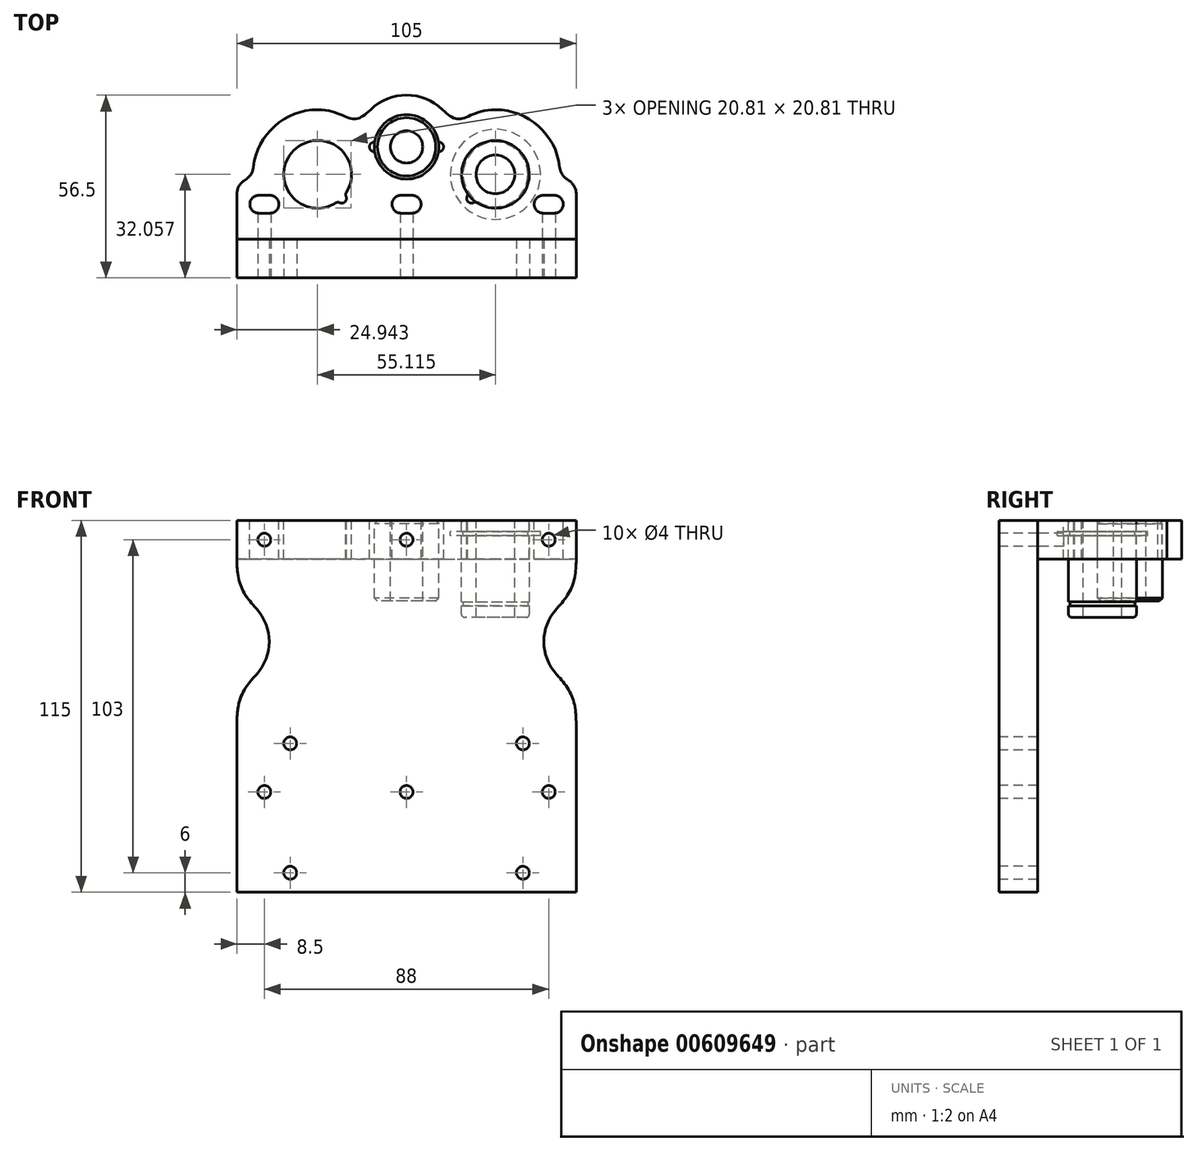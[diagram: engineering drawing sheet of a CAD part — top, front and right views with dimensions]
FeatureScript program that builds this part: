
annotation { "Feature Type Name" : "Feature", "Feature Type Description" : "" }
export const myFeature = defineFeature(function(context is Context, id is Id, definition is map)
    precondition{}
    {
        {
            var Q0;
            Q0=qCreatedBy(makeId("Front.planeOp"),FACE);
            var sketch = newSketch(context, id + "F0", { "sketchPlane" : qUnion([Q0])});
            skLineSegment(sketch, "E0.bottom", {"start": v(-52.5, 0) * mm, "end": v(52.5, 0) * mm});
            skLineSegment(sketch, "E0.top", {"start": v(-52.5, 90) * mm, "end": v(52.5, 90) * mm});
            skLineSegment(sketch, "E0.left", {"start": v(-52.5, 0) * mm, "end": v(-52.5, 90) * mm});
            skLineSegment(sketch, "E0.right", {"start": v(52.5, 0) * mm, "end": v(52.5, 90) * mm});
            skSolve(sketch);
        }
        {
            var Q0;
            Q0=qSketchRegion(id+"F0",true);
            extrude(context, id + "F1", {"entities" : qUnion([Q0]), "oppositeDirection" : true, "depth" : 12 * mm, "offsetDistance" : 25 * mm});
        }
        {
            var Q0;
            Q0=makeQuery(id+"F1.opExtrude","SWEPT_FACE",FACE,{"disambiguationData":[OSD([sQuery(id+"F0.wireOp",EDGE,"E0.top")])]});
            var sketch = newSketch(context, id + "F2", { "sketchPlane" : qUnion([Q0])});
            skLineSegment(sketch, "E1.top", {"start": v(27.5, 52) * mm, "end": v(11.12, 52) * mm, "construction": true});
            skLineSegment(sketch, "E2", {"start": v(0, 12) * mm, "end": v(0, 52) * mm, "construction": true});
            skPoint(sketch, "E3.centerSnap0", {"position": v(0, 32) * mm});
            skArc(sketch, "E4.filletArc", {"start": v(47.5, 32) * mm, "mid": v(41.64, 46.14) * mm, "end": v(27.5, 52) * mm});
            skArc(sketch, "E5.filletArc", {"start": v(-27.5, 52) * mm, "mid": v(-41.64, 46.14) * mm, "end": v(-47.5, 32) * mm});
            skArc(sketch, "E6", {"start": v(21.8, 23.22) * mm, "mid": v(34.9, 39.4) * mm, "end": v(18.72, 26.3) * mm});
            skArc(sketch, "E7.MirrorC", {"start": v(-21.8, 23.22) * mm, "mid": v(-34.9, 39.4) * mm, "end": v(-18.72, 26.3) * mm});
            skArc(sketch, "E8", {"start": v(11.12, 52) * mm, "mid": v(0, 56.5) * mm, "end": v(-11.12, 52) * mm});
            skArc(sketch, "E9", {"start": v(-9.74, 38.33) * mm, "mid": v(0, 30.53) * mm, "end": v(9.74, 38.33) * mm});
            skLineSegment(sketch, "E10", {"start": v(47.5, 12) * mm, "end": v(-47.5, 12) * mm});
            skLineSegment(sketch, "E11.bottom", {"start": v(47.5, 32) * mm, "end": v(52.5, 28.5) * mm});
            skLineSegment(sketch, "E11.top", {"start": v(47.5, 12) * mm, "end": v(52.5, 12) * mm});
            skLineSegment(sketch, "E11.right", {"start": v(52.5, 28.5) * mm, "end": v(52.5, 12) * mm});
            skLineSegment(sketch, "E12.bottom", {"start": v(42.25, 25.5) * mm, "end": v(45.75, 25.5) * mm});
            skLineSegment(sketch, "E12.top", {"start": v(42.25, 20) * mm, "end": v(45.75, 20) * mm});
            skArc(sketch, "E13", {"start": v(42.25, 25.5) * mm, "mid": v(39.5, 22.75) * mm, "end": v(42.25, 20) * mm});
            skArc(sketch, "E14", {"start": v(45.75, 20) * mm, "mid": v(48.5, 22.75) * mm, "end": v(45.75, 25.5) * mm});
            skArc(sketch, "E15.MirrorCS", {"start": v(-42.25, 25.5) * mm, "mid": v(-39.5, 22.75) * mm, "end": v(-42.25, 20) * mm});
            skLineSegment(sketch, "E16.MirrorCS", {"start": v(-42.25, 25.5) * mm, "end": v(-45.75, 25.5) * mm});
            skLineSegment(sketch, "E17.MirrorCS", {"start": v(-42.25, 20) * mm, "end": v(-45.75, 20) * mm});
            skArc(sketch, "E18.MirrorCS", {"start": v(-45.75, 20) * mm, "mid": v(-48.5, 22.75) * mm, "end": v(-45.75, 25.5) * mm});
            skLineSegment(sketch, "E19.MirrorCS", {"start": v(-47.5, 32) * mm, "end": v(-52.5, 28.5) * mm});
            skLineSegment(sketch, "E20.MirrorCS", {"start": v(-52.5, 28.5) * mm, "end": v(-52.5, 12) * mm});
            skLineSegment(sketch, "E21.MirrorCS", {"start": v(-47.5, 12) * mm, "end": v(-52.5, 12) * mm});
            skLineSegment(sketch, "E22.bottom", {"start": v(-1.75, 25.5) * mm, "end": v(1.75, 25.5) * mm});
            skLineSegment(sketch, "E22.top", {"start": v(-1.75, 20) * mm, "end": v(1.75, 20) * mm});
            skArc(sketch, "E23", {"start": v(-1.75, 25.5) * mm, "mid": v(-4.5, 22.75) * mm, "end": v(-1.75, 20) * mm});
            skArc(sketch, "E24", {"start": v(1.75, 20) * mm, "mid": v(4.5, 22.75) * mm, "end": v(1.75, 25.5) * mm});
            skLineSegment(sketch, "E25", {"start": v(-1.75, 22.75) * mm, "end": v(1.75, 22.75) * mm, "construction": true});
            skPoint(sketch, "E26", {"position": v(0, 22.75) * mm});
            skLineSegment(sketch, "E27", {"start": v(-44, 25.5) * mm, "end": v(-44, 20) * mm, "construction": true});
            skLineSegment(sketch, "E28", {"start": v(44, 20) * mm, "end": v(44, 25.5) * mm, "construction": true});
            skLineSegment(sketch, "E29.trimOffspring", {"start": v(-11.12, 52) * mm, "end": v(-27.5, 52) * mm, "construction": true});
            skFitSpline(sketch, "E30", {"points": [v(11.12, 52) * mm, v(16.56, 49.16) * mm, v(27.5, 52) * mm], "startDerivative": vector(14.38, -13.9) * mm, "endDerivative": vector(29.13, 0) * mm});
            skFitSpline(sketch, "E31.MirrorCS", {"points": [v(-11.12, 52) * mm, v(-16.56, 49.16) * mm, v(-27.5, 52) * mm], "startDerivative": vector(-14.38, -13.9) * mm, "endDerivative": vector(-29.13, 0) * mm});
            skLineSegment(sketch, "E32", {"start": v(-11.12, 52) * mm, "end": v(11.12, 52) * mm, "construction": true});
            skArc(sketch, "E33", {"start": v(-10.42, 41.93) * mm, "mid": v(-11.47, 40.5) * mm, "end": v(-10.42, 39.07) * mm});
            skArc(sketch, "E34.MirrorC", {"start": v(10.42, 41.93) * mm, "mid": v(11.47, 40.5) * mm, "end": v(10.42, 39.07) * mm});
            skArc(sketch, "E35.trimOffspring", {"start": v(9.74, 42.67) * mm, "mid": v(0, 50.48) * mm, "end": v(-9.74, 42.67) * mm});
            skPoint(sketch, "E36.visualSharp", {"position": v(-9.86, 42) * mm});
            skArc(sketch, "E36.filletArc", {"start": v(-10.42, 41.93) * mm, "mid": v(-9.98, 42.21) * mm, "end": v(-9.74, 42.67) * mm});
            skPoint(sketch, "E37.visualSharp", {"position": v(-9.86, 39) * mm});
            skArc(sketch, "E37.filletArc", {"start": v(-9.74, 38.33) * mm, "mid": v(-9.98, 38.79) * mm, "end": v(-10.42, 39.07) * mm});
            skPoint(sketch, "E38.visualSharp", {"position": v(9.86, 39) * mm});
            skArc(sketch, "E38.filletArc", {"start": v(10.42, 39.07) * mm, "mid": v(9.98, 38.79) * mm, "end": v(9.74, 38.33) * mm});
            skPoint(sketch, "E39.visualSharp", {"position": v(9.86, 42) * mm});
            skArc(sketch, "E39.filletArc", {"start": v(9.74, 42.67) * mm, "mid": v(9.98, 42.21) * mm, "end": v(10.42, 41.93) * mm});
            skArc(sketch, "E40", {"start": v(-20.79, 23.26) * mm, "mid": v(-19.03, 23.53) * mm, "end": v(-18.76, 25.29) * mm});
            skLineSegment(sketch, "E41", {"start": v(-27.5, 32) * mm, "end": v(-20.1, 24.6) * mm, "construction": true});
            skArc(sketch, "E42.MirrorCS", {"start": v(20.79, 23.26) * mm, "mid": v(19.03, 23.53) * mm, "end": v(18.76, 25.29) * mm});
            skPoint(sketch, "E43.visualSharp", {"position": v(-21.23, 23.61) * mm});
            skArc(sketch, "E43.filletArc", {"start": v(-20.79, 23.26) * mm, "mid": v(-21.3, 23.38) * mm, "end": v(-21.8, 23.22) * mm});
            skPoint(sketch, "E44.visualSharp", {"position": v(-19.11, 25.73) * mm});
            skArc(sketch, "E44.filletArc", {"start": v(-18.72, 26.3) * mm, "mid": v(-18.88, 25.8) * mm, "end": v(-18.76, 25.29) * mm});
            skPoint(sketch, "E45.visualSharp", {"position": v(19.11, 25.73) * mm});
            skArc(sketch, "E45.filletArc", {"start": v(18.76, 25.29) * mm, "mid": v(18.88, 25.8) * mm, "end": v(18.72, 26.3) * mm});
            skPoint(sketch, "E46.visualSharp", {"position": v(21.23, 23.61) * mm});
            skArc(sketch, "E46.filletArc", {"start": v(21.8, 23.22) * mm, "mid": v(21.3, 23.38) * mm, "end": v(20.79, 23.26) * mm});
            skSolve(sketch);
        }
        {
            var Q0;
            Q0=qSketchRegion(id+"F2",true);
            extrude(context, id + "F3", {"entities" : qUnion([Q0]), "oppositeDirection" : true, "depth" : 12 * mm, "offsetDistance" : 25 * mm});
        }
        {
            var Q0;
            Q0=makeQuery(id+"F3.opExtrude","SWEPT_EDGE",EDGE,{"disambiguationData":[OSD([sQuery(id+"F2.wireOp",EDGE,"E5.filletArc"),sQuery(id+"F2.wireOp",EDGE,"E19.MirrorCS")])]});
            var Q1;
            Q1=makeQuery(id+"F3.opExtrude","SWEPT_EDGE",EDGE,{"disambiguationData":[OSD([sQuery(id+"F2.wireOp",EDGE,"E19.MirrorCS"),sQuery(id+"F2.wireOp",EDGE,"E20.MirrorCS")])]});
            var Q2;
            Q2=makeQuery(id+"F3.opExtrude","SWEPT_EDGE",EDGE,{"disambiguationData":[OSD([sQuery(id+"F2.wireOp",EDGE,"E4.filletArc"),sQuery(id+"F2.wireOp",EDGE,"E11.bottom")])]});
            var Q3;
            Q3=makeQuery(id+"F3.opExtrude","SWEPT_EDGE",EDGE,{"disambiguationData":[OSD([sQuery(id+"F2.wireOp",EDGE,"E11.bottom"),sQuery(id+"F2.wireOp",EDGE,"E11.right")])]});
            fillet(context, id + "F4", {"entities" : qUnion([Q0, Q1, Q2, Q3]), "radius" : 5 * mm, "tangentPropagation" : true, "allowEdgeOverflow" : false});
        }
        {
            var Q0;
            Q0=makeQuery(id+"F3.opExtrude","CAP_FACE",FACE,{"disambiguationData":[OSD([sQuery(id+"F2.wireOp",EDGE,"E1.bottom"),sQuery(id+"F2.wireOp",EDGE,"E1.top"),sQuery(id+"F2.wireOp",EDGE,"E1.left"),sQuery(id+"F2.wireOp",EDGE,"E1.right"),sQuery(id+"F2.wireOp",EDGE,"E3"),sQuery(id+"F2.wireOp",EDGE,"E4.filletArc"),sQuery(id+"F2.wireOp",EDGE,"E5.filletArc"),sQuery(id+"F2.wireOp",EDGE,"cdc9c876-c57f-4e5e-8f0d-edd7876a0e1e0.MirrorC")])],"isStart":true});
            var sketch = newSketch(context, id + "F5", { "sketchPlane" : qUnion([Q0])});
            skCircle(sketch, "E47", {"center": v(27.5, 32) * mm, "radius": 10.5 * mm});
            skCircle(sketch, "E48", {"center": v(27.5, 32) * mm, "radius": 6 * mm});
            skSolve(sketch);
        }
        {
            var Q0;
            Q0=qSketchRegion(id+"F5",true);
            extrude(context, id + "F6", {"entities" : qUnion([Q0]), "oppositeDirection" : true, "depth" : 30 * mm, "offsetDistance" : 25 * mm});
        }
        {
            var Q0;
            Q0=makeQuery(id+"F6.opExtrude","CAP_FACE",FACE,{"disambiguationData":[OSD([sQuery(id+"F5.wireOp",EDGE,"E47"),sQuery(id+"F5.wireOp",EDGE,"E48")])],"isStart":true});
            var sketch = newSketch(context, id + "F7", { "sketchPlane" : qUnion([Q0])});
            skCircle(sketch, "E49", {"center": v(27.5, 32) * mm, "radius": 10 * mm});
            skCircle(sketch, "E50", {"center": v(27.5, 32) * mm, "radius": 13.95 * mm});
            skSolve(sketch);
        }
        {
            var Q0;
            Q0=qSketchRegion(id+"F7",true);
            extrude(context, id + "F8", {"entities" : qUnion([Q0]), "operationType" : NewBodyOperationType.REMOVE, "oppositeDirection" : true, "depth" : 4.8 * mm, "offsetDistance" : 25 * mm, "hasSecondDirection" : true, "secondDirectionOppositeDirection" : true, "secondDirectionDepth" : 3.5 * mm});
        }
        {
            var Q0;
            Q0=makeQuery(id+"F6.opExtrude","CAP_FACE",FACE,{"disambiguationData":[OSD([sQuery(id+"F5.wireOp",EDGE,"E47"),sQuery(id+"F5.wireOp",EDGE,"E48")])],"isStart":false});
            var sketch = newSketch(context, id + "F9", { "sketchPlane" : qUnion([Q0])});
            skCircle(sketch, "E51", {"center": v(27.5, -32) * mm, "radius": 10 * mm});
            skCircle(sketch, "E52", {"center": v(27.5, -32) * mm, "radius": 14.7 * mm});
            skSolve(sketch);
        }
        {
            var Q0;
            Q0=qSketchRegion(id+"F9",true);
            extrude(context, id + "F10", {"entities" : qUnion([Q0]), "operationType" : NewBodyOperationType.REMOVE, "oppositeDirection" : true, "depth" : 4.8 * mm, "offsetDistance" : 25 * mm, "hasSecondDirection" : true, "secondDirectionOppositeDirection" : true, "secondDirectionDepth" : 3.5 * mm});
        }
        {
            var Q0;
            Q0=makeQuery(id+"F6.opExtrude","CAP_EDGE",EDGE,{"disambiguationData":[OSD([sQuery(id+"F5.wireOp",EDGE,"E47")])],"isStart":true});
            var Q1;
            Q1=makeQuery(id+"F6.opExtrude","CAP_EDGE",EDGE,{"disambiguationData":[OSD([sQuery(id+"F5.wireOp",EDGE,"E47")])],"isStart":false});
            fillet(context, id + "F11", {"entities" : qUnion([Q0, Q1]), "radius" : 1 * mm, "tangentPropagation" : true, "allowEdgeOverflow" : false});
        }
        {
            var Q0;
            Q0=makeQuery(id+"F1.opExtrude","CAP_FACE",FACE,{"disambiguationData":[OSD([sQuery(id+"F0.wireOp",EDGE,"E0.bottom"),sQuery(id+"F0.wireOp",EDGE,"E0.top"),sQuery(id+"F0.wireOp",EDGE,"E0.left"),sQuery(id+"F0.wireOp",EDGE,"E0.right")])],"isStart":true});
            var sketch = newSketch(context, id + "F12", { "sketchPlane" : qUnion([Q0])});
            skLineSegment(sketch, "E53.bottom", {"start": v(-52.5, 0) * mm, "end": v(52.5, 0) * mm});
            skLineSegment(sketch, "E53.top", {"start": v(-52.5, -25) * mm, "end": v(52.5, -25) * mm});
            skLineSegment(sketch, "E53.left", {"start": v(-52.5, 0) * mm, "end": v(-52.5, -25) * mm});
            skLineSegment(sketch, "E53.right", {"start": v(52.5, 0) * mm, "end": v(52.5, -25) * mm});
            skSolve(sketch);
        }
        {
            var Q0;
            Q0=qSketchRegion(id+"F12",true);
            var Q1;
            Q1=makeQuery(id+"F1.opExtrude","CAP_FACE",FACE,{"disambiguationData":[OSD([sQuery(id+"F0.wireOp",EDGE,"E0.bottom"),sQuery(id+"F0.wireOp",EDGE,"E0.top"),sQuery(id+"F0.wireOp",EDGE,"E0.left"),sQuery(id+"F0.wireOp",EDGE,"E0.right")])],"isStart":false});
            extrude(context, id + "F13", {"entities" : qUnion([Q0]), "operationType" : NewBodyOperationType.ADD, "endBound" : BoundingType.UP_TO_SURFACE, "oppositeDirection" : true, "depth" : 18 * mm, "endBoundEntityFace" : qUnion([Q1]), "offsetDistance" : 25 * mm});
        }
        {
            var Q0;
            Q0=makeQuery(id+"F3.opExtrude","CAP_FACE",FACE,{"disambiguationData":[OSD([sQuery(id+"F2.wireOp",EDGE,"E1.bottom"),sQuery(id+"F2.wireOp",EDGE,"E1.top"),sQuery(id+"F2.wireOp",EDGE,"E1.left"),sQuery(id+"F2.wireOp",EDGE,"E1.right"),sQuery(id+"F2.wireOp",EDGE,"E4.filletArc"),sQuery(id+"F2.wireOp",EDGE,"E5.filletArc"),sQuery(id+"F2.wireOp",EDGE,"E6"),sQuery(id+"F2.wireOp",EDGE,"E7.MirrorC")])],"isStart":true});
            var sketch = newSketch(context, id + "F14", { "sketchPlane" : qUnion([Q0])});
            skCircle(sketch, "E54", {"center": v(0, 40.5) * mm, "radius": 10 * mm});
            skCircle(sketch, "E55", {"center": v(0, 40.5) * mm, "radius": 5 * mm});
            skSolve(sketch);
        }
        {
            var Q0;
            Q0=qSketchRegion(id+"F14",true);
            extrude(context, id + "F15", {"entities" : qUnion([Q0]), "oppositeDirection" : true, "depth" : 25 * mm, "offsetDistance" : 25 * mm});
        }
        {
            var Q0;
            Q0=makeQuery(id+"F1.opExtrude","CAP_FACE",FACE,{"disambiguationData":[OSD([sQuery(id+"F0.wireOp",EDGE,"E0.bottom"),sQuery(id+"F0.wireOp",EDGE,"E0.top"),sQuery(id+"F0.wireOp",EDGE,"E0.left"),sQuery(id+"F0.wireOp",EDGE,"E0.right")])],"isStart":true});
            var sketch = newSketch(context, id + "F16", { "sketchPlane" : qUnion([Q0])});
            skCircle(sketch, "E56", {"center": v(-44, 84) * mm, "radius": 2 * mm});
            skCircle(sketch, "E57", {"center": v(44, 84) * mm, "radius": 2 * mm});
            skCircle(sketch, "E58", {"center": v(0, 84) * mm, "radius": 2 * mm});
            skLineSegment(sketch, "E59", {"start": v(-52.5, 45) * mm, "end": v(53.36, 45) * mm, "construction": true});
            skCircle(sketch, "E60.MirrorC", {"center": v(44, 6) * mm, "radius": 2 * mm});
            skCircle(sketch, "E61.MirrorC", {"center": v(0, 6) * mm, "radius": 2 * mm});
            skCircle(sketch, "E62.MirrorC", {"center": v(-44, 6) * mm, "radius": 2 * mm});
            skCircle(sketch, "E63", {"center": v(-36, -19) * mm, "radius": 2 * mm});
            skCircle(sketch, "E64", {"center": v(36, -19) * mm, "radius": 2 * mm});
            skCircle(sketch, "E65.0.1.0", {"center": v(36, 21) * mm, "radius": 2 * mm});
            skCircle(sketch, "E65.0.1.1", {"center": v(-36, 21) * mm, "radius": 2 * mm});
            skLineSegment(sketch, "E65.direction1", {"start": v(-36, -19) * mm, "end": v(-14, -19) * mm, "construction": true});
            skLineSegment(sketch, "E65.direction2", {"start": v(-36, -19) * mm, "end": v(-36, 21) * mm, "construction": true});
            skSolve(sketch);
        }
        {
            var Q0;
            Q0 = qSketchRegion(id + "F16", true);
            extrude(context, id + "F17", {"entities" : qUnion([Q0]), "operationType" : NewBodyOperationType.REMOVE, "oppositeDirection" : true, "depth" : 25 * mm, "offsetDistance" : 25 * mm});
        }
        {
            var Q0;
            Q0=makeQuery(id+"F15.opExtrude","CAP_EDGE",EDGE,{"disambiguationData":[OSD([sQuery(id+"F14.wireOp",EDGE,"E54")])],"isStart":false});
            var Q1;
            Q1=makeQuery(id+"F15.opExtrude","CAP_EDGE",EDGE,{"disambiguationData":[OSD([sQuery(id+"F14.wireOp",EDGE,"E54")])],"isStart":true});
            chamfer(context, id + "F18", {"entities" : qUnion([Q0, Q1]), "width" : 1 * mm, "tangentPropagation" : true});
        }
        {
            var Q0;
            Q0=makeQuery(id+"F13.boolean.opBoolean","MERGE",FACE,{"derivedFrom":[makeQuery(id+"F1.opExtrude","CAP_FACE",FACE,{"disambiguationData":[OSD([sQuery(id+"F0.wireOp",EDGE,"E0.bottom"),sQuery(id+"F0.wireOp",EDGE,"E0.top"),sQuery(id+"F0.wireOp",EDGE,"E0.left"),sQuery(id+"F0.wireOp",EDGE,"E0.right")])],"isStart":true}),makeQuery(id+"F13.opExtrude","CAP_FACE",FACE,{"disambiguationData":[OSD([sQuery(id+"F12.wireOp",EDGE,"E53.bottom"),sQuery(id+"F12.wireOp",EDGE,"E53.top"),sQuery(id+"F12.wireOp",EDGE,"E53.left"),sQuery(id+"F12.wireOp",EDGE,"E53.right")])],"isStart":true})]});
            var sketch = newSketch(context, id + "F19", { "sketchPlane" : qUnion([Q0])});
            skCircle(sketch, "E66", {"center": v(-57.5, 52.5) * mm, "radius": 15 * mm});
            skLineSegment(sketch, "E67", {"start": v(-52.5, 27) * mm, "end": v(52.5, 27) * mm, "construction": true});
            skLineSegment(sketch, "E68", {"start": v(0, 27) * mm, "end": v(0, 90) * mm, "construction": true});
            skCircle(sketch, "E69.MirrorC", {"center": v(57.5, 52.5) * mm, "radius": 15 * mm});
            skSolve(sketch);
        }
        {
            var Q0;
            Q0 = qSketchRegion(id + "F19", true);
            extrude(context, id + "F20", {"entities" : qUnion([Q0]), "operationType" : NewBodyOperationType.REMOVE, "oppositeDirection" : true, "depth" : 25 * mm, "offsetDistance" : 25 * mm});
        }
        {
            var Q0;
            Q0=makeQuery(id+"F20.boolean.opBoolean","INTERSECT",EDGE,{"disambiguationData":[OD(0.0)],"derivedFrom":[makeQuery(id+"F13.boolean.opBoolean","MERGE",FACE,{"derivedFrom":[makeQuery(id+"F1.opExtrude","SWEPT_FACE",FACE,{"disambiguationData":[OSD([sQuery(id+"F0.wireOp",EDGE,"E0.left")])]}),makeQuery(id+"F13.opExtrude","SWEPT_FACE",FACE,{"disambiguationData":[OSD([sQuery(id+"F12.wireOp",EDGE,"E53.left")])]})]}),makeQuery(id+"F20.opExtrude","SWEPT_FACE",FACE,{"disambiguationData":[OSD([sQuery(id+"F19.wireOp",EDGE,"E66")])]})]});
            var Q1;
            Q1=makeQuery(id+"F20.boolean.opBoolean","INTERSECT",EDGE,{"disambiguationData":[OD(1.0)],"derivedFrom":[makeQuery(id+"F13.boolean.opBoolean","MERGE",FACE,{"derivedFrom":[makeQuery(id+"F1.opExtrude","SWEPT_FACE",FACE,{"disambiguationData":[OSD([sQuery(id+"F0.wireOp",EDGE,"E0.left")])]}),makeQuery(id+"F13.opExtrude","SWEPT_FACE",FACE,{"disambiguationData":[OSD([sQuery(id+"F12.wireOp",EDGE,"E53.left")])]})]}),makeQuery(id+"F20.opExtrude","SWEPT_FACE",FACE,{"disambiguationData":[OSD([sQuery(id+"F19.wireOp",EDGE,"E66")])]})]});
            var Q2;
            Q2=makeQuery(id+"F20.boolean.opBoolean","INTERSECT",EDGE,{"disambiguationData":[OD(0.0)],"derivedFrom":[makeQuery(id+"F13.boolean.opBoolean","MERGE",FACE,{"derivedFrom":[makeQuery(id+"F1.opExtrude","SWEPT_FACE",FACE,{"disambiguationData":[OSD([sQuery(id+"F0.wireOp",EDGE,"E0.right")])]}),makeQuery(id+"F13.opExtrude","SWEPT_FACE",FACE,{"disambiguationData":[OSD([sQuery(id+"F12.wireOp",EDGE,"E53.right")])]})]}),makeQuery(id+"F20.opExtrude","SWEPT_FACE",FACE,{"disambiguationData":[OSD([sQuery(id+"F19.wireOp",EDGE,"E69.MirrorC")])]})]});
            var Q3;
            Q3=makeQuery(id+"F20.boolean.opBoolean","INTERSECT",EDGE,{"disambiguationData":[OD(1.0)],"derivedFrom":[makeQuery(id+"F13.boolean.opBoolean","MERGE",FACE,{"derivedFrom":[makeQuery(id+"F1.opExtrude","SWEPT_FACE",FACE,{"disambiguationData":[OSD([sQuery(id+"F0.wireOp",EDGE,"E0.right")])]}),makeQuery(id+"F13.opExtrude","SWEPT_FACE",FACE,{"disambiguationData":[OSD([sQuery(id+"F12.wireOp",EDGE,"E53.right")])]})]}),makeQuery(id+"F20.opExtrude","SWEPT_FACE",FACE,{"disambiguationData":[OSD([sQuery(id+"F19.wireOp",EDGE,"E69.MirrorC")])]})]});
            fillet(context, id + "F21", {"entities" : qUnion([Q0, Q1, Q2, Q3]), "radius" : 23 * mm, "tangentPropagation" : true, "rho" : 0.6, "crossSection" : FilletCrossSection.CONIC, "allowEdgeOverflow" : false});
        }
    });
